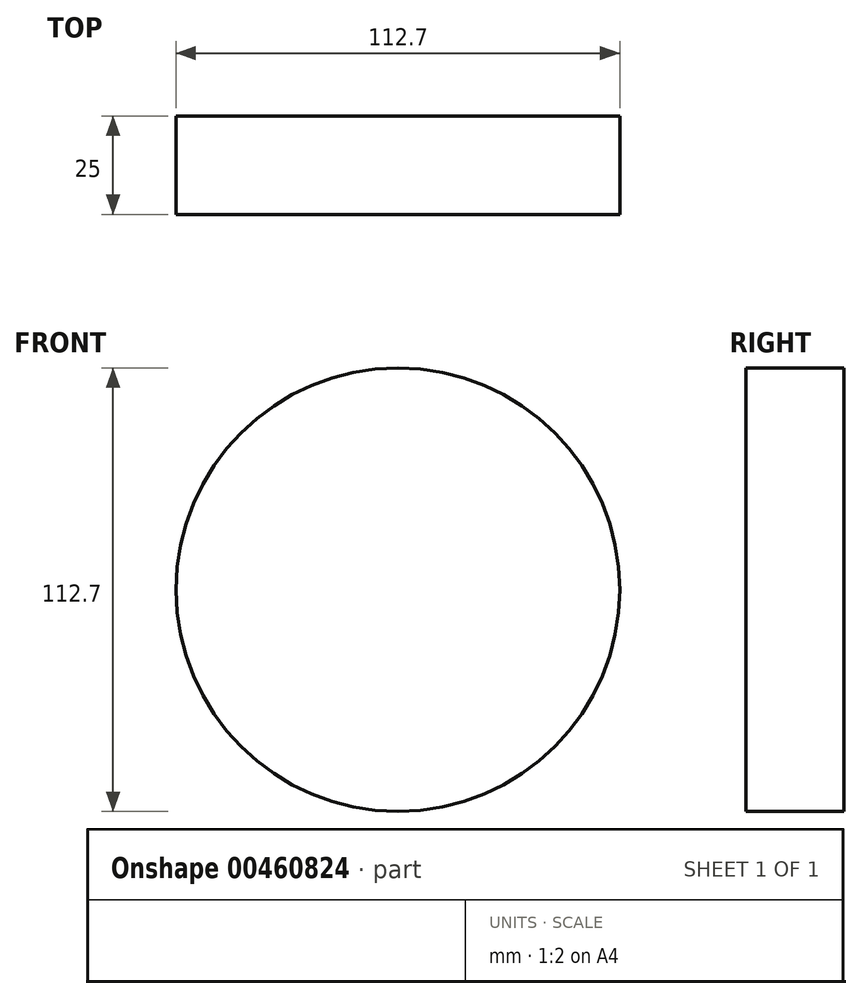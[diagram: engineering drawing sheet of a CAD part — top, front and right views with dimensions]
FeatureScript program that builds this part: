
annotation { "Feature Type Name" : "Feature", "Feature Type Description" : "" }
export const myFeature = defineFeature(function(context is Context, id is Id, definition is map)
    precondition{}
    {
        {
            var Q0;
            Q0=qCreatedBy(makeId("Front.planeOp"),FACE);
            var sketch = newSketch(context, id + "F0", { "sketchPlane" : qUnion([Q0])});
            skCircle(sketch, "E0", {"center": v(0, 0) * mm, "radius": 56.35 * mm});
            skSolve(sketch);
        }
        {
            var Q0;
            Q0=makeQuery(id+"F0.imprint","IMPRINT",FACE,{"disambiguationData":[TD([[makeQuery(id+"F0.imprint","IMPRINT",EDGE,{"derivedFrom":sQuery(id+"F0.wireOp",EDGE,"E0")}),1.0]])]});
            extrude(context, id + "F1", {"entities" : qUnion([Q0]), "depth" : 25 * mm});
        }
    });
